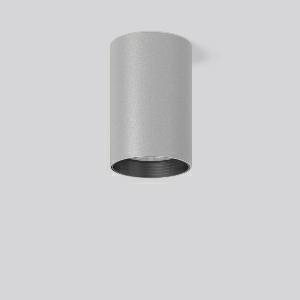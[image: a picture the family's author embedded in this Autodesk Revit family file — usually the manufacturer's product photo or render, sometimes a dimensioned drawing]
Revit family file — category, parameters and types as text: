
# Revit family: heledon_maxi_a_931229_004_76_48da
name_source: partatom
category: Lighting Fixtures
units: mm (PartAtom-declared; Revit-internal decimal feet)

## family parameters
Cut with Voids When Loaded = No
Host = Face
Light Source = No
Part Type = Normal
Room Calculation Point = No
Round Connector Dimension = Use Diameter
Shared = No

## types (1)
- HELEDON maxi A (1 x LED Modul 930, 3600 lm, 3000)
    Apparent Load = 35 VA
    Approval mark = CE
    CIE Flux Codes = 96 100 100 100 100
    Color Rendering = 90
    Color Temperature = 3000
    Default Elevation = 1800 mm
    Description = Series: HELEDON maxi
Cylindrical surface-mounted downlight. Housing: die-cast aluminium, powder-coated. Internal ceiling frame polycarbonate with bayonet mounting. Black plastic ring and recessed LED to prevent glare from the side. Optical assembly with lens made of plastic (polycarbonate) for the best homogeneous light distribution - can be changed without tools. Best colour rendering index Ra>90. Suitable for Ceiling mounting. Easy installation with a separate ceiling frame with bayonet mounting and plug connection. Driver integrated. Connected via plug-in connector. High quality converter without flickering and stroboscopic effect. The following accessories can be mounted without use of tools: interchangeable lenses, decorative glasses, honeycomb louvre, clear and frosted diffusers, white interchangeable plastic ring. 
Colour: silver
Diameter: 123 mm
Height: 183 mm
Lamp: LED
Socket: without socket
Colour temperature: 3000K
Colour rendering index (CRI): 92
System power: 35 W
Rated luminous flux: 3600 lm
Luminous efficiency: 103 lm/W
Control gear: Converter, dimmable, DALI
Protection class: I
Type of protection: IP 20
    Height = 183 mm
    Lamp = 1 x LED Modul 930
    Lamp Light Flux = 3600 lm
    Lamp count = 1
    Length = 123 mm
    Lifetime = 50000 h
    Luminous efficacy = 103 lm/W
    Manufacturer = RZB
    ModVariant = No
    Model = 931229.004.76
    Mounting Place = Ceiling
    Mounting Type = Surface mounted
    Number of Poles = 1
    OnlyDefault = Yes
    Power Factor = 1
    Product Name = HELEDON maxi A
    Product group = Surface mounted downlights
    ProductGroupID = 302
    Protection Class = Protection class I
    Protection Degree = IP 20
    RLX_Detail_Level = 1
    RLX_Emergency_Light_Flux = 0 lm
    RLX_Emergency_Type = 0
    RLX_Emergency_Type_DB = No
    RlxData = <blob elided: 98377 chars, md5=5d2bfb9f>
    Socket = socket
    Standby Power = 0 W
    System Light Flux = 3600 lm
    System Power = 35 W
    Type Comments = Product without accessories
    Type Image = 931193.004.jpg
    URL = http://relux.com
    VarID = ---
    Voltage = 230 V
    Voltage Range = 220-240 V
    Weight = 0.00 kg
    Width = 0 mm  [stored 0 ft]

note: [stored X ft] marks values corroborated as IEEE doubles in the binary element streams (Revit-internal decimal feet)

## geometry (parser evidence)
native form markers: Blend x4, Sweep x11
no freeform markers — native parametric forms only
